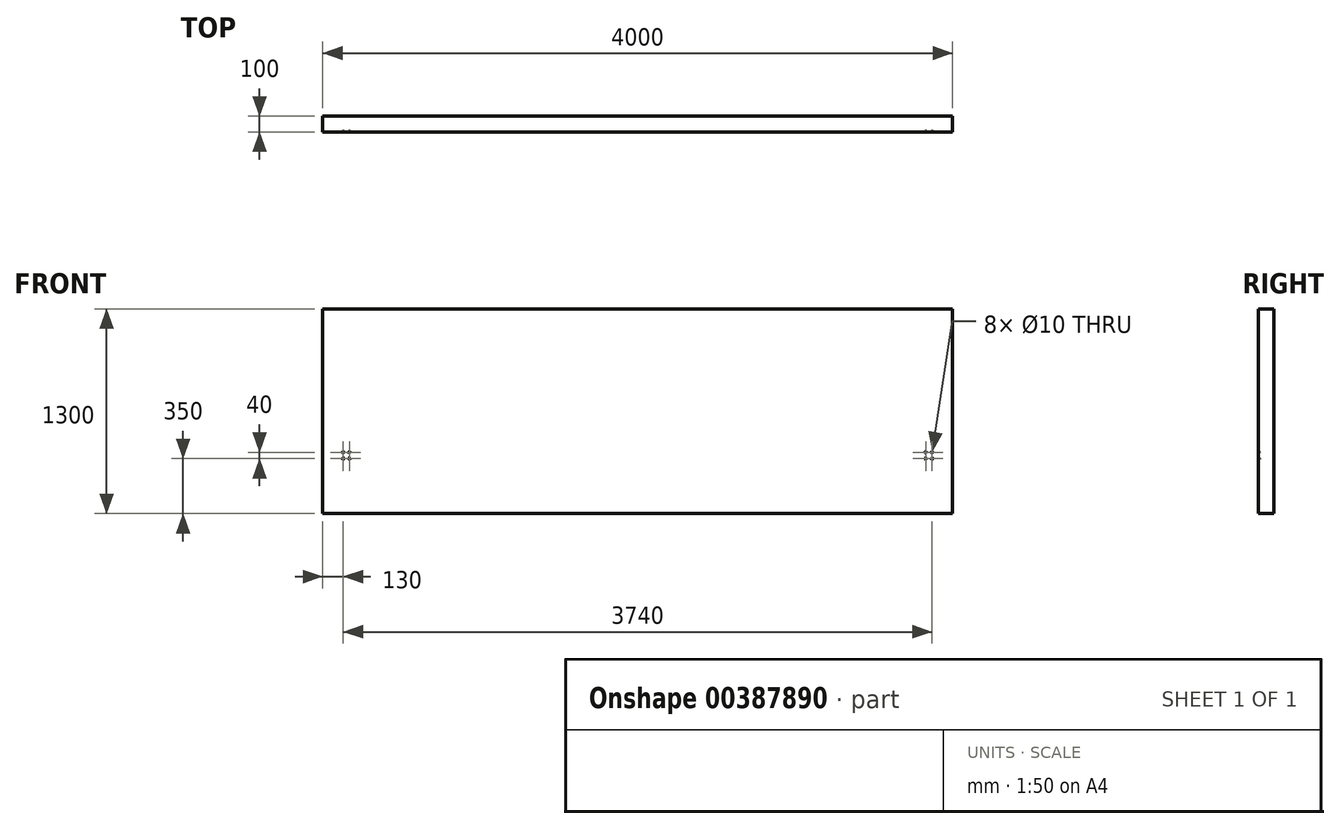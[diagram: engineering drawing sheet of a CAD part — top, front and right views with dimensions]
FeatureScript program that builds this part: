
annotation { "Feature Type Name" : "Feature", "Feature Type Description" : "" }
export const myFeature = defineFeature(function(context is Context, id is Id, definition is map)
    precondition{}
    {
        {
            var Q0;
            Q0=qCreatedBy(makeId("Front.planeOp"),FACE);
            var sketch = newSketch(context, id + "F0", { "sketchPlane" : qUnion([Q0])});
            skLineSegment(sketch, "E0.bottom", {"start": v(-2000, 650) * mm, "end": v(2000, 650) * mm});
            skLineSegment(sketch, "E0.top", {"start": v(-2000, -650) * mm, "end": v(2000, -650) * mm});
            skLineSegment(sketch, "E0.left", {"start": v(-2000, 650) * mm, "end": v(-2000, -650) * mm});
            skLineSegment(sketch, "E0.right", {"start": v(2000, 650) * mm, "end": v(2000, -650) * mm});
            skPoint(sketch, "E0.middle", {"position": v(0, 0) * mm});
            skLineSegment(sketch, "E1", {"start": v(0, 398.71) * mm, "end": v(0, -377.7) * mm, "construction": true});
            skSolve(sketch);
        }
        {
            var Q0;
            Q0=makeQuery(id+"F0.imprint","IMPRINT",FACE,{"disambiguationData":[TD([[makeQuery(id+"F0.imprint","IMPRINT",EDGE,{"derivedFrom":sQuery(id+"F0.wireOp",EDGE,"E0.bottom")}),-1.0]])]});
            extrude(context, id + "F1", {"entities" : qUnion([Q0]), "depth" : 100 * mm, "symmetric" : true});
        }
        {
            var Q0;
            Q0=makeQuery(id+"F1.opExtrude","CAP_FACE",FACE,{"disambiguationData":[OSD([sQuery(id+"F0.wireOp",EDGE,"E0.bottom"),sQuery(id+"F0.wireOp",EDGE,"E0.top"),sQuery(id+"F0.wireOp",EDGE,"E0.left"),sQuery(id+"F0.wireOp",EDGE,"E0.right")])],"isStart":false});
            var sketch = newSketch(context, id + "F2", { "sketchPlane" : qUnion([Q0])});
            skLineSegment(sketch, "E2.bottom", {"start": v(-2000, -650) * mm, "end": v(-1850, -650) * mm});
            skLineSegment(sketch, "E2.top", {"start": v(-2000, -280) * mm, "end": v(-1850, -280) * mm});
            skLineSegment(sketch, "E2.left", {"start": v(-2000, -650) * mm, "end": v(-2000, -280) * mm});
            skLineSegment(sketch, "E2.right", {"start": v(-1850, -650) * mm, "end": v(-1850, -280) * mm});
            skLineSegment(sketch, "E3.bottom", {"start": v(-1870, -260) * mm, "end": v(-1830, -260) * mm});
            skLineSegment(sketch, "E3.top", {"start": v(-1870, -300) * mm, "end": v(-1830, -300) * mm});
            skLineSegment(sketch, "E3.left", {"start": v(-1870, -260) * mm, "end": v(-1870, -300) * mm});
            skLineSegment(sketch, "E3.right", {"start": v(-1830, -260) * mm, "end": v(-1830, -300) * mm});
            skPoint(sketch, "E3.middle", {"position": v(-1850, -280) * mm});
            skLineSegment(sketch, "E4", {"start": v(2000, -650) * mm, "end": v(1850, -650) * mm});
            skLineSegment(sketch, "E5", {"start": v(1850, -650) * mm, "end": v(1850, -280) * mm});
            skLineSegment(sketch, "E6.bottom", {"start": v(1830, -260) * mm, "end": v(1870, -260) * mm});
            skLineSegment(sketch, "E6.top", {"start": v(1830, -300) * mm, "end": v(1870, -300) * mm});
            skLineSegment(sketch, "E6.left", {"start": v(1830, -260) * mm, "end": v(1830, -300) * mm});
            skLineSegment(sketch, "E6.right", {"start": v(1870, -260) * mm, "end": v(1870, -300) * mm});
            skPoint(sketch, "E6.middle", {"position": v(1850, -280) * mm});
            skSolve(sketch);
        }
        {
            var Q0;
            Q0=sQuery(id+"F2.wireOp",VERTEX,"E3.left.start");
            var Q1;
            Q1=sQuery(id+"F2.wireOp",VERTEX,"E3.right.start");
            var Q2;
            Q2=sQuery(id+"F2.wireOp",VERTEX,"E3.right.end");
            var Q3;
            Q3=sQuery(id+"F2.wireOp",VERTEX,"E3.left.end");
            var Q4;
            Q4=sQuery(id+"F2.wireOp",VERTEX,"E6.bottom.start");
            var Q5;
            Q5=sQuery(id+"F2.wireOp",VERTEX,"E6.right.start");
            var Q6;
            Q6=sQuery(id+"F2.wireOp",VERTEX,"E6.top.end");
            var Q7;
            Q7=sQuery(id+"F2.wireOp",VERTEX,"E6.top.start");
            var Q8;
            Q8=makeQuery(id+"F1.opExtrude","SWEPT_BODY",BODY,{"disambiguationData":[OSD([sQuery(id+"F0.wireOp",EDGE,"E0.bottom"),sQuery(id+"F0.wireOp",EDGE,"E0.top"),sQuery(id+"F0.wireOp",EDGE,"E0.left"),sQuery(id+"F0.wireOp",EDGE,"E0.right")])]});
            hole(context, id + "F3", {"style" : HoleStyle.SIMPLE, "endStyle" : HoleEndStyle.BLIND, "holeDiameter" : 10 * mm, "holeDepth" : 10 * mm, "isTappedThrough" : true, "tappedDepth" : 12 * mm, "tapClearance" : 3, "locations" : qUnion([Q0, Q1, Q2, Q3, Q4, Q5, Q6, Q7]), "scope" : qUnion([Q8])});
        }
    });
